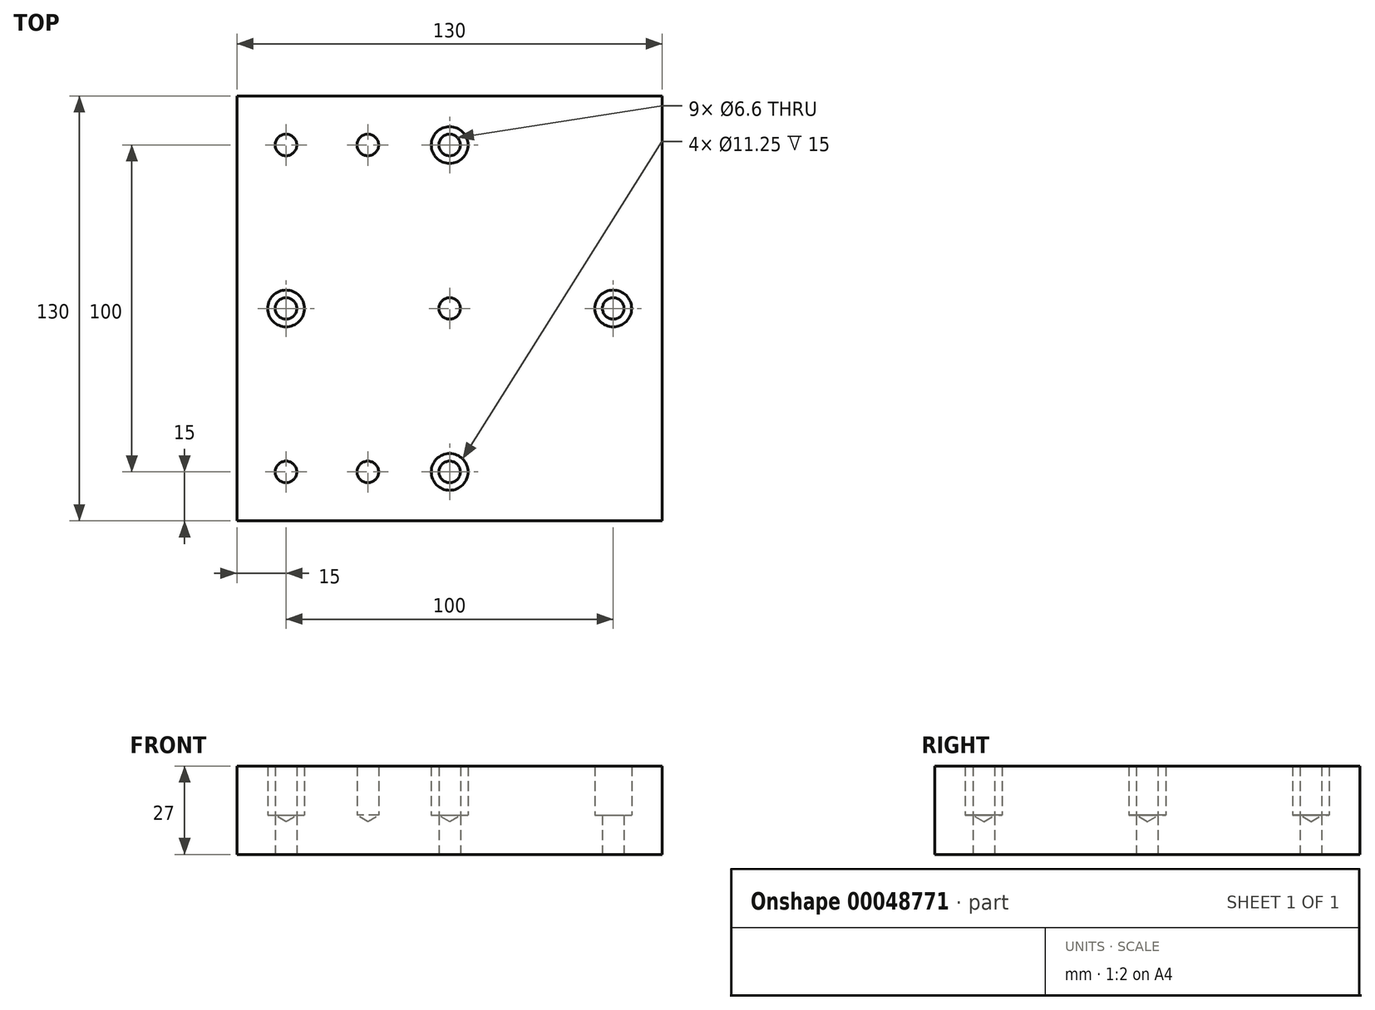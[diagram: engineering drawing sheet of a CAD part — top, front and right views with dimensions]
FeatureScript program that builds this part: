
annotation { "Feature Type Name" : "Feature", "Feature Type Description" : "" }
export const myFeature = defineFeature(function(context is Context, id is Id, definition is map)
    precondition{}
    {
        {
            var Q0;
            Q0=qCreatedBy(makeId("Top.planeOp"),FACE);
            var sketch = newSketch(context, id + "F0", { "sketchPlane" : qUnion([Q0])});
            skLineSegment(sketch, "E0.bottom", {"start": v(65, -65) * mm, "end": v(-65, -65) * mm});
            skLineSegment(sketch, "E0.top", {"start": v(65, 65) * mm, "end": v(-65, 65) * mm});
            skLineSegment(sketch, "E0.left", {"start": v(65, -65) * mm, "end": v(65, 65) * mm});
            skLineSegment(sketch, "E0.right", {"start": v(-65, -65) * mm, "end": v(-65, 65) * mm});
            skPoint(sketch, "E0.middle", {"position": v(0, 0) * mm});
            skSolve(sketch);
        }
        {
            var Q0;
            Q0=makeQuery(id+"F0.imprint","IMPRINT",FACE,{"disambiguationData":[TD([[makeQuery(id+"F0.imprint","IMPRINT",EDGE,{"derivedFrom":sQuery(id+"F0.wireOp",EDGE,"E0.bottom")}),-1.0]])]});
            extrude(context, id + "F1", {"entities" : qUnion([Q0]), "depth" : 27 * mm});
        }
        {
            var Q0;
            Q0=makeQuery(id+"F1.opExtrude","CAP_FACE",FACE,{"disambiguationData":[OSD([sQuery(id+"F0.wireOp",EDGE,"E0.bottom"),sQuery(id+"F0.wireOp",EDGE,"E0.top"),sQuery(id+"F0.wireOp",EDGE,"E0.left"),sQuery(id+"F0.wireOp",EDGE,"E0.right")])],"isStart":false});
            var sketch = newSketch(context, id + "F2", { "sketchPlane" : qUnion([Q0])});
            skPoint(sketch, "E1", {"position": v(0, 0) * mm});
            skCircle(sketch, "E2", {"center": v(0, 0) * mm, "radius": 50 * mm, "construction": true});
            skPoint(sketch, "E3", {"position": v(50, 0) * mm});
            skPoint(sketch, "E4", {"position": v(0, 50) * mm});
            skPoint(sketch, "E5", {"position": v(-50, 0) * mm});
            skPoint(sketch, "E6", {"position": v(0, -50) * mm});
            skPoint(sketch, "E7", {"position": v(-25, 50) * mm});
            skPoint(sketch, "E8.0.1.0", {"position": v(-25, -50) * mm});
            skPoint(sketch, "E8.1.0.0", {"position": v(-50, 50) * mm});
            skPoint(sketch, "E8.1.1.0", {"position": v(-50, -50) * mm});
            skLineSegment(sketch, "E8.direction1", {"start": v(-25, 50) * mm, "end": v(-50, 50) * mm, "construction": true});
            skLineSegment(sketch, "E8.direction2", {"start": v(-25, 50) * mm, "end": v(-25, -50) * mm, "construction": true});
            skSolve(sketch);
        }
        {
            var Q0;
            Q0=sQuery(id+"F2.wireOp",VERTEX,"E4");
            var Q1;
            Q1=sQuery(id+"F2.wireOp",VERTEX,"E5");
            var Q2;
            Q2=sQuery(id+"F2.wireOp",VERTEX,"E6");
            var Q3;
            Q3=sQuery(id+"F2.wireOp",VERTEX,"E3");
            var Q4;
            Q4=makeQuery(id+"F1.opExtrude","SWEPT_BODY",BODY,{"disambiguationData":[OSD([sQuery(id+"F0.wireOp",EDGE,"E0.bottom"),sQuery(id+"F0.wireOp",EDGE,"E0.top"),sQuery(id+"F0.wireOp",EDGE,"E0.left"),sQuery(id+"F0.wireOp",EDGE,"E0.right")])]});
            hole(context, id + "F3", {"style" : HoleStyle.C_BORE, "endStyle" : HoleEndStyle.THROUGH, "holeDiameter" : 6.6 * mm, "cBoreDiameter" : 11.25 * mm, "cBoreDepth" : 15 * mm, "locations" : qUnion([Q0, Q1, Q2, Q3]), "scope" : qUnion([Q4]), "isTappedThrough" : true, "startStyle" : HoleStartStyle.PART});
        }
        {
            var Q0;
            Q0=sQuery(id+"F2.wireOp",VERTEX,"E7");
            var Q1;
            Q1=sQuery(id+"F2.wireOp",VERTEX,"E8.0.1.0");
            var Q2;
            Q2=sQuery(id+"F2.wireOp",VERTEX,"E8.1.1.0");
            var Q3;
            Q3=sQuery(id+"F2.wireOp",VERTEX,"E8.1.0.0");
            var Q4;
            Q4=sQuery(id+"F2.wireOp",VERTEX,"E1");
            var Q5;
            Q5=makeQuery(id+"F1.opExtrude","SWEPT_BODY",BODY,{"disambiguationData":[OSD([sQuery(id+"F0.wireOp",EDGE,"E0.bottom"),sQuery(id+"F0.wireOp",EDGE,"E0.top"),sQuery(id+"F0.wireOp",EDGE,"E0.left"),sQuery(id+"F0.wireOp",EDGE,"E0.right")])]});
            hole(context, id + "F4", {"style" : HoleStyle.SIMPLE, "endStyle" : HoleEndStyle.BLIND, "standardTappedOrClearance" : lookupTablePath({ "standard" : "ISO", "fit" : "Normal", "size" : "M6", "type" : "Clearance" }), "standardBlindInLast" : lookupTablePath({ "fit" : "Standard", "standard" : "ISO", "size" : "M6", "type" : "Clearance" }), "holeDiameter" : 6.6 * mm, "holeDepth" : 15 * mm, "locations" : qUnion([Q0, Q1, Q2, Q3, Q4]), "scope" : qUnion([Q5]), "startStyle" : HoleStartStyle.PART});
        }
    });
